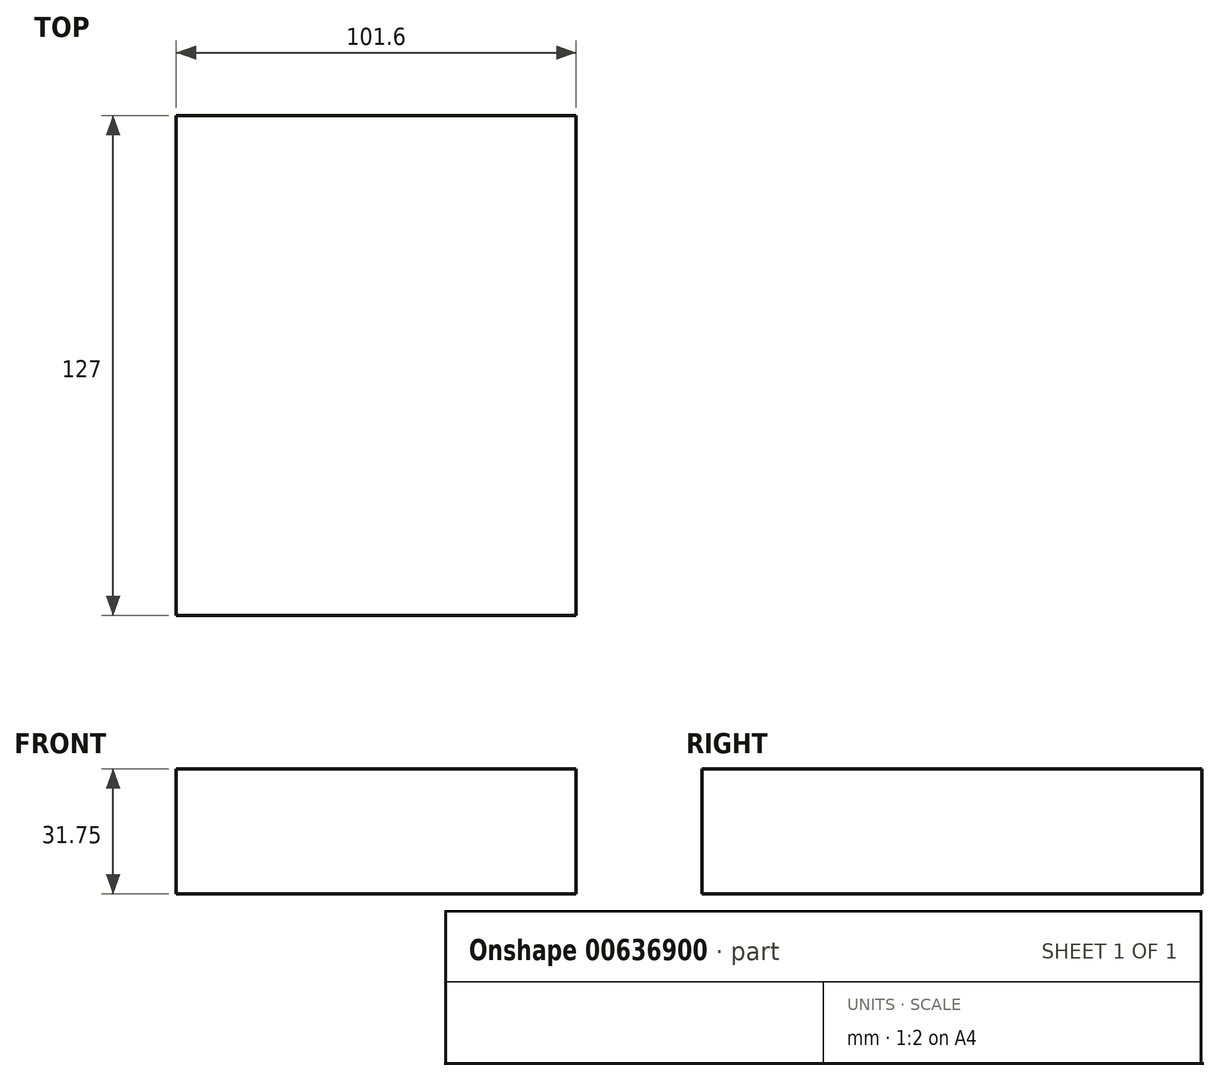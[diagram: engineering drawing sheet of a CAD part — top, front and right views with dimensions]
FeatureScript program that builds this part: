
annotation { "Feature Type Name" : "Feature", "Feature Type Description" : "" }
export const myFeature = defineFeature(function(context is Context, id is Id, definition is map)
    precondition{}
    {
        {
            var Q0;
            Q0=qCreatedBy(makeId("Front.planeOp"),FACE);
            var sketch = newSketch(context, id + "F0", { "sketchPlane" : qUnion([Q0])});
            skLineSegment(sketch, "E0.bottom", {"start": v(0, 0) * mm, "end": v(101.6, 0) * mm});
            skLineSegment(sketch, "E0.top", {"start": v(0, 31.75) * mm, "end": v(101.6, 31.75) * mm});
            skLineSegment(sketch, "E0.left", {"start": v(0, 0) * mm, "end": v(0, 31.75) * mm});
            skLineSegment(sketch, "E0.right", {"start": v(101.6, 0) * mm, "end": v(101.6, 31.75) * mm});
            skLineSegment(sketch, "E1", {"start": v(101.6, 31.75) * mm, "end": v(101.6, 57.15) * mm});
            skArc(sketch, "E2", {"start": v(101.6, 57.15) * mm, "mid": v(109.78, 76.9) * mm, "end": v(129.54, 85.1) * mm});
            skLineSegment(sketch, "E3", {"start": v(129.54, 85.1) * mm, "end": v(154.94, 85.1) * mm});
            skLineSegment(sketch, "E4.0", {"start": v(129.54, 102.87) * mm, "end": v(154.94, 102.87) * mm});
            skArc(sketch, "E4.1", {"start": v(83.82, 57.15) * mm, "mid": v(97.21, 89.48) * mm, "end": v(129.54, 102.87) * mm});
            skLineSegment(sketch, "E4.2", {"start": v(83.82, 31.75) * mm, "end": v(83.82, 57.15) * mm});
            skLineSegment(sketch, "E5.bottom", {"start": v(132.34, 107.4) * mm, "end": v(183.14, 107.4) * mm});
            skLineSegment(sketch, "E5.top", {"start": v(132.34, 78.83) * mm, "end": v(183.14, 78.83) * mm});
            skLineSegment(sketch, "E5.left", {"start": v(132.34, 107.4) * mm, "end": v(132.34, 78.83) * mm});
            skLineSegment(sketch, "E5.right", {"start": v(183.14, 107.4) * mm, "end": v(183.14, 78.83) * mm});
            skLineSegment(sketch, "E6", {"start": v(154.94, 102.87) * mm, "end": v(154.94, 85.1) * mm});
            skLineSegment(sketch, "E7", {"start": v(157.74, 107.4) * mm, "end": v(157.74, 78.83) * mm});
            skFitSpline(sketch, "E8", {"points": [v(0, 31.75) * mm, v(129.54, 102.87) * mm], "startDerivative": vector(27.91, 139.75) * mm, "endDerivative": vector(204.84, -8.88) * mm});
            skSolve(sketch);
        }
        {
            var Q0;
            Q0=makeQuery(id+"F0.imprint","IMPRINT",FACE,{"disambiguationData":[TD([[makeQuery(id+"F0.imprint","IMPRINT",EDGE,{"derivedFrom":sQuery(id+"F0.wireOp",EDGE,"E0.bottom")}),1.0]])]});
            extrude(context, id + "F1", {"entities" : qUnion([Q0]), "endBound" : BoundingType.SYMMETRIC, "depth" : 127 * mm, "offsetDistance" : 25.4 * mm});
        }
    });
